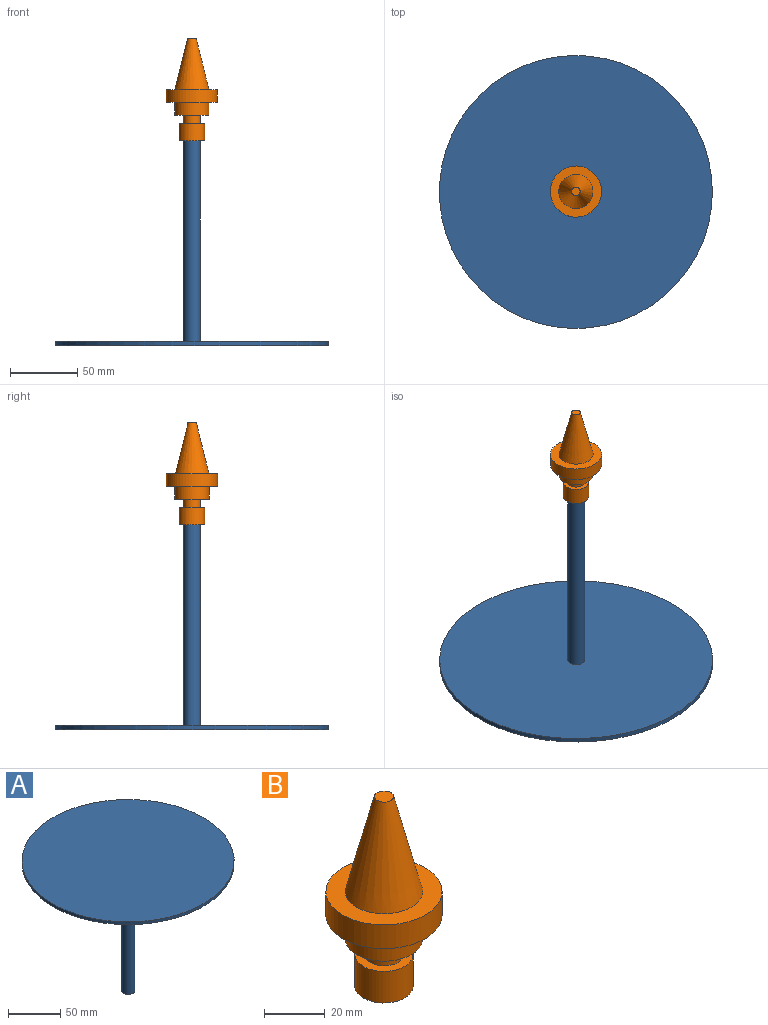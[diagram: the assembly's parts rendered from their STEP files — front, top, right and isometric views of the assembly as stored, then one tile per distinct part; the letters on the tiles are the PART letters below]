
ASSEMBLY  parts=2 mates=1
PART A: 5 faces, bbox 203.2x203.2x152.4 mm
  f0: cylinder r=6.35mm len=149.23mm, axis (0,0,-1), area 5953.8mm2, adj f1,f3
  f1: plane 12.7x12.7mm, normal (0,0,-1), area 126.7mm2, adj f0
  f2: cylinder r=101.6mm len=203.2mm, axis (0,0,1), area 2026.8mm2, adj f3,f4
  f3: plane 203.2x203.2mm, normal (0,0,-1), area 32302.6mm2, adj f0,f2
  f4: plane 203.2x203.2mm, normal (0,0,1), area 32429.3mm2, adj f2
PART B: 11 faces, bbox 38.1x38.1x76.2 mm
  f0: plane 6.35x6.35mm, normal (0,0,1), area 31.7mm2, adj f1
  f1: cone r=3.17mm half-angle=14deg, axis (0,0,-1), area 1958.6mm2, adj f0,f2
  f2: plane 38.1x38.1mm, normal (0,0,1), area 633.4mm2, adj f1,f3
  f3: cylinder r=19.05mm len=38.1mm, axis (0,0,-1), area 1140.1mm2, adj f2,f4
  f4: plane 38.1x38.1mm, normal (0,0,-1), area 633.4mm2, adj f3,f5
  f5: cylinder r=12.7mm len=25.4mm, axis (0,0,-1), area 760.1mm2, adj f4,f6
  f6: plane 25.4x25.4mm, normal (0,0,-1), area 380mm2, adj f5,f7
  f7: cylinder r=6.35mm len=12.7mm, axis (0,0,-1), area 253.4mm2, adj f6,f8
  f8: plane 19.05x19.05mm, normal (0,0,1), area 158.3mm2, adj f7,f9
  f9: cylinder r=9.53mm len=19.05mm, axis (0,0,-1), area 760.1mm2, adj f8,f10
  f10: plane 19.05x19.05mm, normal (0,0,-1), area 285mm2, adj f9
PLACE A rot(axis=(1,0,0),180deg) t=(0,0,-38.1)mm
PLACE B at identity
MATE fastened A.f0 <-> B.f1  axis (0,0,1) through (0,0,-38.1)mm
